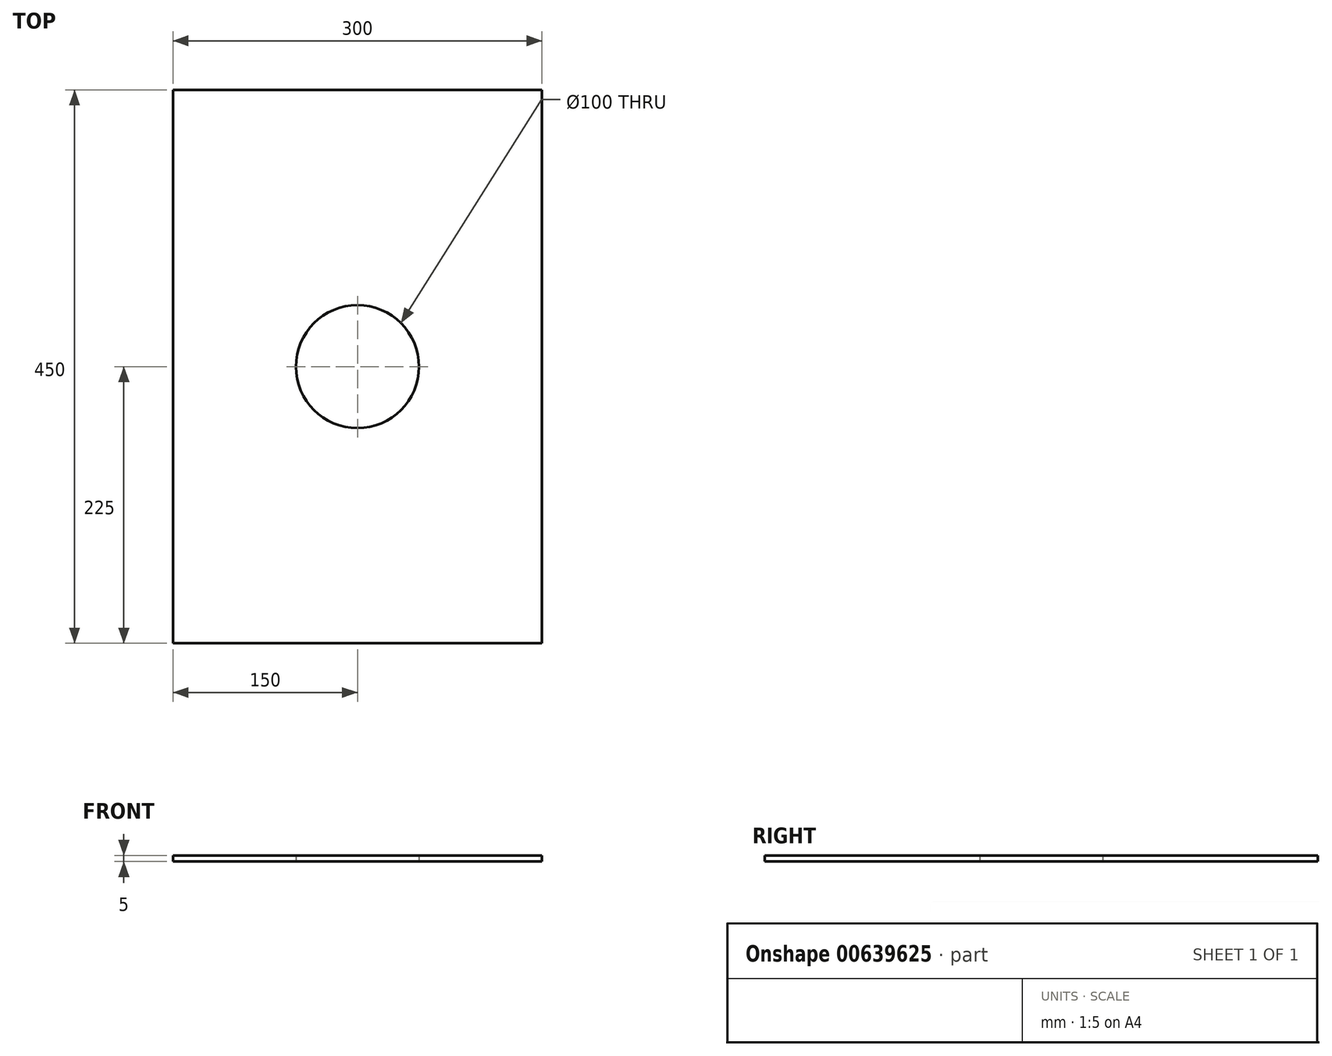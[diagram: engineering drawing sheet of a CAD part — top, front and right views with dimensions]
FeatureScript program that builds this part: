
annotation { "Feature Type Name" : "Feature", "Feature Type Description" : "" }
export const myFeature = defineFeature(function(context is Context, id is Id, definition is map)
    precondition{}
    {
        {
            var Q0;
            Q0=qCreatedBy(makeId("Top.planeOp"),FACE);
            var sketch = newSketch(context, id + "F0", { "sketchPlane" : qUnion([Q0])});
            skLineSegment(sketch, "E0.bottom", {"start": v(-150, 225) * mm, "end": v(150, 225) * mm});
            skLineSegment(sketch, "E0.top", {"start": v(-150, -225) * mm, "end": v(150, -225) * mm});
            skLineSegment(sketch, "E0.left", {"start": v(-150, 225) * mm, "end": v(-150, -225) * mm});
            skLineSegment(sketch, "E0.right", {"start": v(150, 225) * mm, "end": v(150, -225) * mm});
            skPoint(sketch, "E1.endSnap0", {"position": v(0, -225) * mm});
            skLineSegment(sketch, "E2", {"start": v(0, 225) * mm, "end": v(0, -225) * mm, "construction": true});
            skLineSegment(sketch, "E3", {"start": v(-150, 0) * mm, "end": v(150, 0) * mm, "construction": true});
            skSolve(sketch);
        }
        {
            var Q0;
            Q0=makeQuery(id+"F0.imprint","IMPRINT",FACE,{"disambiguationData":[TD([[makeQuery(id+"F0.imprint","IMPRINT",EDGE,{"derivedFrom":sQuery(id+"F0.wireOp",EDGE,"E0.bottom")}),-1.0]])]});
            extrude(context, id + "F1", {"entities" : qUnion([Q0]), "depth" : 5 * mm, "offsetDistance" : 25 * mm});
        }
        {
            var Q0;
            Q0=makeQuery(id+"F1.opExtrude","SWEPT_FACE",FACE,{"disambiguationData":[OSD([sQuery(id+"F0.wireOp",EDGE,"E0.right")])]});
            var sketch = newSketch(context, id + "F2", { "sketchPlane" : qUnion([Q0])});
            skLineSegment(sketch, "E4", {"start": v(225, 5) * mm, "end": v(225, 0) * mm});
            skArc(sketch, "E5", {"start": v(225, 5) * mm, "mid": v(224.33, 2.5) * mm, "end": v(225, 0) * mm});
            skLineSegment(sketch, "E6", {"start": v(-225, 0) * mm, "end": v(-225, 5) * mm});
            skArc(sketch, "E7", {"start": v(-225, 0) * mm, "mid": v(-224.33, 2.5) * mm, "end": v(-225, 5) * mm});
            skSolve(sketch);
        }
        {
            var Q0;
            Q0=makeQuery(id+"F1.opExtrude","CAP_FACE",FACE,{"disambiguationData":[OSD([sQuery(id+"F0.wireOp",EDGE,"E0.bottom"),sQuery(id+"F0.wireOp",EDGE,"E0.top"),sQuery(id+"F0.wireOp",EDGE,"E0.left"),sQuery(id+"F0.wireOp",EDGE,"E0.right")])],"isStart":true});
            var sketch = newSketch(context, id + "F3", { "sketchPlane" : qUnion([Q0])});
            skCircle(sketch, "E8", {"center": v(0, 0) * mm, "radius": 50 * mm});
            skSolve(sketch);
        }
        {
            var Q0;
            Q0=makeQuery(id+"F3.imprint","IMPRINT",FACE,{"disambiguationData":[TD([[makeQuery(id+"F3.imprint","IMPRINT",EDGE,{"derivedFrom":sQuery(id+"F3.wireOp",EDGE,"E8")}),1.0]])]});
            var Q1;
            Q1=sQuery(id+"F3.wireOp",EDGE,"E8");
            extrude(context, id + "F4", {"entities" : qUnion([Q0]), "operationType" : NewBodyOperationType.REMOVE, "surfaceEntities" : qUnion([Q1]), "oppositeDirection" : true, "depth" : 25 * mm, "offsetDistance" : 25 * mm});
        }
    });
